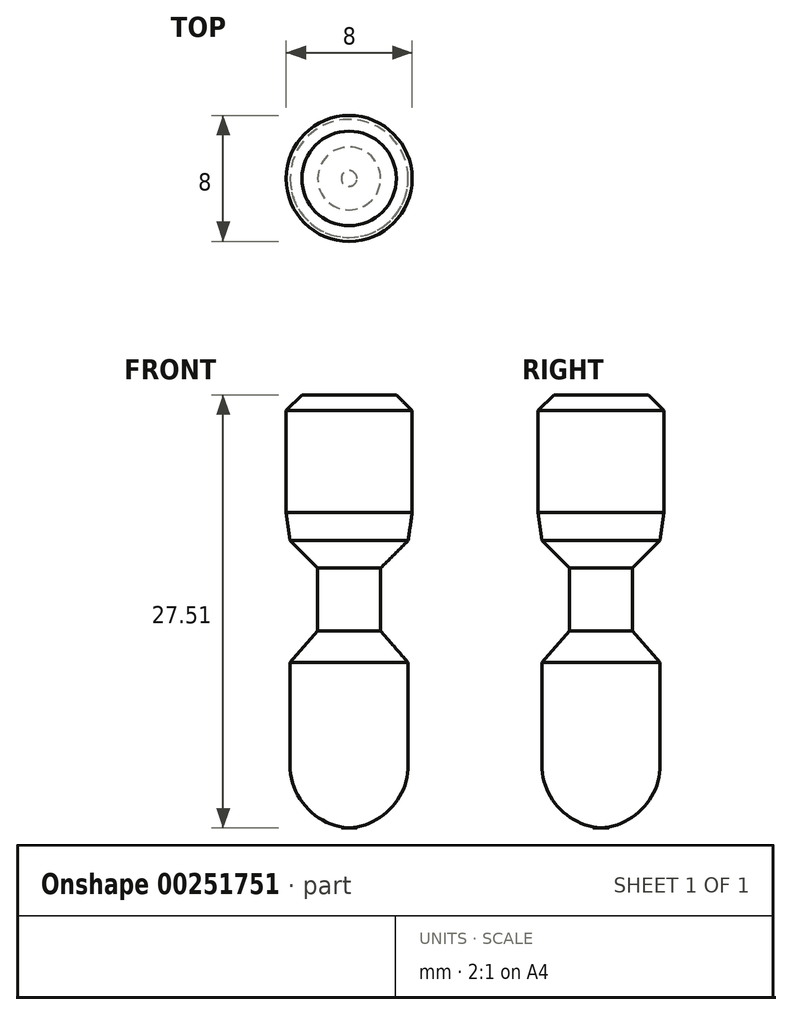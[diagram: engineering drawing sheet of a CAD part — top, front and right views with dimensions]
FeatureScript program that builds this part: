
annotation { "Feature Type Name" : "Feature", "Feature Type Description" : "" }
export const myFeature = defineFeature(function(context is Context, id is Id, definition is map)
    precondition{}
    {
        {
            var Q0;
            Q0=qCreatedBy(makeId("Front.planeOp"),FACE);
            var sketch = newSketch(context, id + "F0", { "sketchPlane" : qUnion([Q0])});
            skLineSegment(sketch, "E0", {"start": v(0, 0) * mm, "end": v(4, 0) * mm});
            skLineSegment(sketch, "E1", {"start": v(4, 0) * mm, "end": v(4, -7.47) * mm});
            skLineSegment(sketch, "E2", {"start": v(4, -7.47) * mm, "end": v(3.75, -9.25) * mm});
            skLineSegment(sketch, "E3", {"start": v(3.75, -9.25) * mm, "end": v(2, -11) * mm});
            skPoint(sketch, "E4.end.orphan", {"position": v(0, -15.4) * mm});
            skLineSegment(sketch, "E5", {"start": v(2, -11) * mm, "end": v(2, -15) * mm});
            skLineSegment(sketch, "E6", {"start": v(2, -15) * mm, "end": v(3.75, -17) * mm});
            skLineSegment(sketch, "E7", {"start": v(3.75, -17) * mm, "end": v(3.75, -23.5) * mm});
            skArc(sketch, "E8", {"start": v(0, -27.5) * mm, "mid": v(2.67, -26.25) * mm, "end": v(3.75, -23.5) * mm});
            skLineSegment(sketch, "E9", {"start": v(0, 0) * mm, "end": v(0, -27.5) * mm});
            skSolve(sketch);
        }
        {
            var Q0;
            Q0=makeQuery(id+"F0.imprint","IMPRINT",FACE,{"disambiguationData":[TD([[makeQuery(id+"F0.imprint","IMPRINT",EDGE,{"derivedFrom":sQuery(id+"F0.wireOp",EDGE,"E0")}),-1.0]])]});
            var Q1;
            Q1=sQuery(id+"F0.wireOp",EDGE,"E9");
            revolve(context, id + "F1", {"entities" : qUnion([Q0]), "axis" : qUnion([Q1]), "revolveType" : RevolveType.FULL});
        }
        {
            var Q0;
            Q0=makeQuery(id+"F1.opRevolve","SWEPT_EDGE",EDGE,{"disambiguationData":[OSD([sQuery(id+"F0.wireOp",EDGE,"E0"),sQuery(id+"F0.wireOp",EDGE,"E1")])]});
            chamfer(context, id + "F2", {"entities" : qUnion([Q0]), "width" : 1 * mm, "tangentPropagation" : true});
        }
    });
